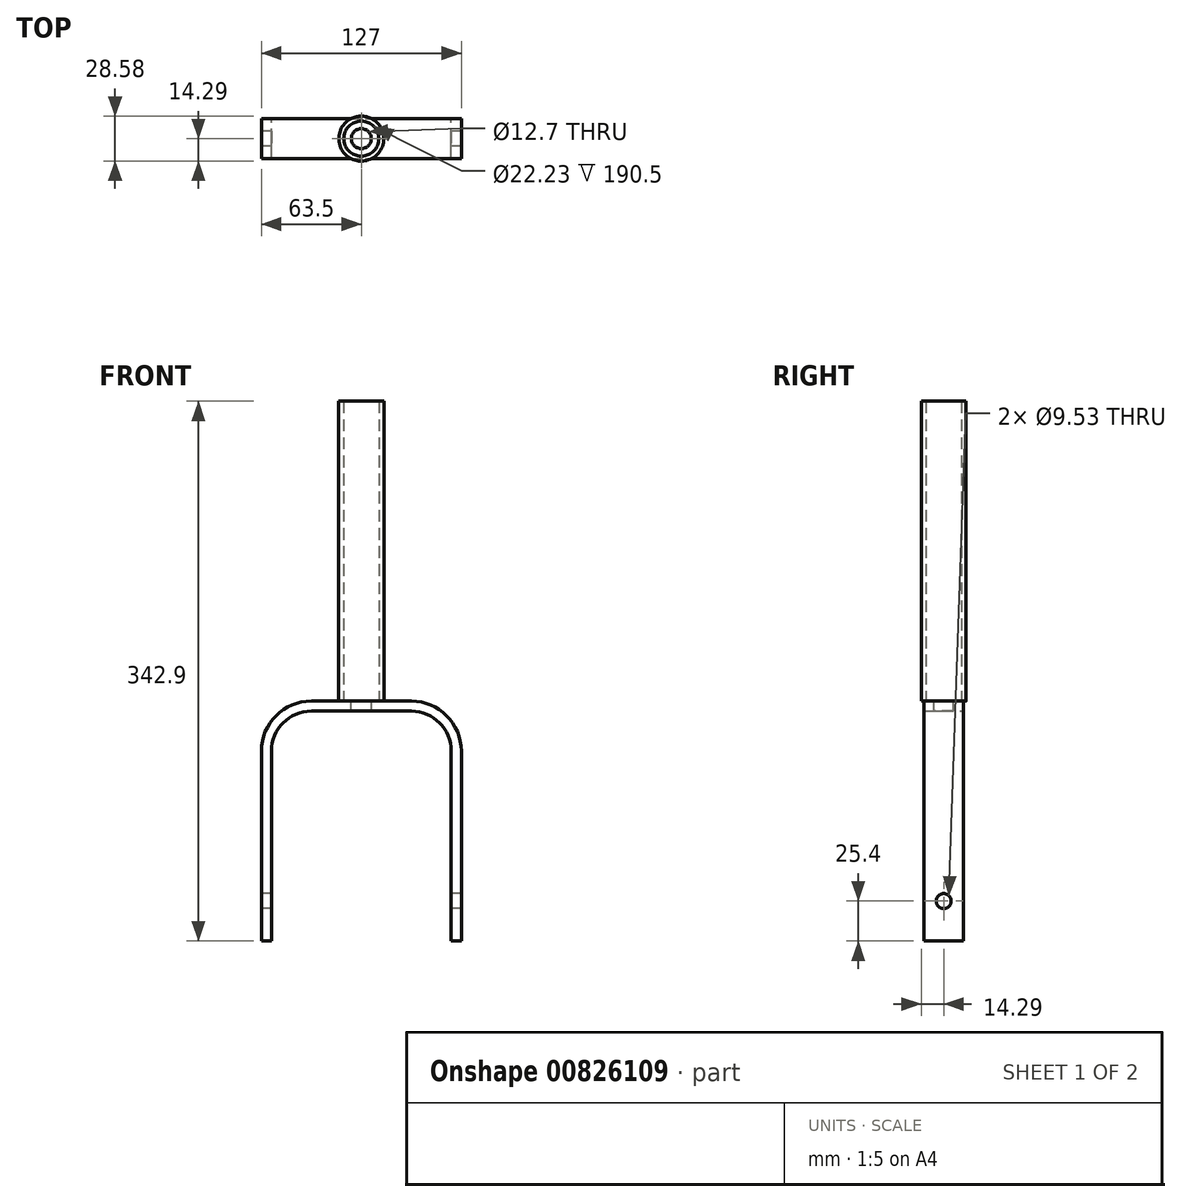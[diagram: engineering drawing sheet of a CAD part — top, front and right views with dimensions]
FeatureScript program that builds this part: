
annotation { "Feature Type Name" : "Feature", "Feature Type Description" : "" }
export const myFeature = defineFeature(function(context is Context, id is Id, definition is map)
    precondition{}
    {
        {
            var Q0;
            Q0=qCreatedBy(makeId("Front.planeOp"),FACE);
            var sketch = newSketch(context, id + "F0", { "sketchPlane" : qUnion([Q0])});
            skLineSegment(sketch, "E0", {"start": v(0, 0) * mm, "end": v(0, 152.4) * mm});
            skLineSegment(sketch, "E1.0", {"start": v(6.35, 0) * mm, "end": v(6.35, 146.05) * mm});
            skLineSegment(sketch, "E2", {"start": v(0, 152.4) * mm, "end": v(127, 152.4) * mm});
            skLineSegment(sketch, "E3", {"start": v(6.35, 146.05) * mm, "end": v(120.65, 146.05) * mm});
            skLineSegment(sketch, "E4", {"start": v(120.65, 146.05) * mm, "end": v(120.65, 0) * mm});
            skLineSegment(sketch, "E5", {"start": v(127, 152.4) * mm, "end": v(127, 0) * mm});
            skLineSegment(sketch, "E6", {"start": v(6.35, 0) * mm, "end": v(0, 0) * mm});
            skLineSegment(sketch, "E7", {"start": v(120.65, 0) * mm, "end": v(127, 0) * mm});
            skSolve(sketch);
        }
        {
            var Q0;
            Q0=makeQuery(id+"F0.imprint","IMPRINT",FACE,{"disambiguationData":[TD([[makeQuery(id+"F0.imprint","IMPRINT",EDGE,{"derivedFrom":sQuery(id+"F0.wireOp",EDGE,"E0")}),-1.0]])]});
            extrude(context, id + "F1", {"entities" : qUnion([Q0]), "endBound" : BoundingType.SYMMETRIC, "depth" : 25.4 * mm, "offsetDistance" : 25.4 * mm});
        }
        {
            var Q0;
            Q0=makeQuery(id+"F1.opExtrude","SWEPT_EDGE",EDGE,{"disambiguationData":[OSD([sQuery(id+"F0.wireOp",EDGE,"E1.0"),sQuery(id+"F0.wireOp",EDGE,"E3")])]});
            var Q1;
            Q1=makeQuery(id+"F1.opExtrude","SWEPT_EDGE",EDGE,{"disambiguationData":[OSD([sQuery(id+"F0.wireOp",EDGE,"E3"),sQuery(id+"F0.wireOp",EDGE,"E4")])]});
            fillet(context, id + "F2", {"entities" : qUnion([Q0, Q1]), "radius" : 25.4 * mm, "tangentPropagation" : true, "allowEdgeOverflow" : false});
        }
        {
            var Q0;
            Q0=makeQuery(id+"F1.opExtrude","SWEPT_EDGE",EDGE,{"disambiguationData":[OSD([sQuery(id+"F0.wireOp",EDGE,"E2"),sQuery(id+"F0.wireOp",EDGE,"E5")])]});
            var Q1;
            Q1=makeQuery(id+"F1.opExtrude","SWEPT_EDGE",EDGE,{"disambiguationData":[OSD([sQuery(id+"F0.wireOp",EDGE,"E0"),sQuery(id+"F0.wireOp",EDGE,"E2")])]});
            fillet(context, id + "F3", {"entities" : qUnion([Q0, Q1]), "radius" : 31.75 * mm, "tangentPropagation" : true, "allowEdgeOverflow" : false});
        }
        {
            var Q0;
            Q0=qCreatedBy(makeId("Right.planeOp"),FACE);
            var sketch = newSketch(context, id + "F4", { "sketchPlane" : qUnion([Q0])});
            skPoint(sketch, "E8", {"position": v(0, 25.4) * mm});
            skSolve(sketch);
        }
        {
            var Q0;
            Q0=sQuery(id+"F4.wireOp",VERTEX,"E8");
            var Q1;
            Q1=makeQuery(id+"F1.opExtrude","SWEPT_BODY",BODY,{"disambiguationData":[OSD([sQuery(id+"F0.wireOp",EDGE,"E0"),sQuery(id+"F0.wireOp",EDGE,"E1.0"),sQuery(id+"F0.wireOp",EDGE,"E2"),sQuery(id+"F0.wireOp",EDGE,"E3"),sQuery(id+"F0.wireOp",EDGE,"E4"),sQuery(id+"F0.wireOp",EDGE,"E5"),sQuery(id+"F0.wireOp",EDGE,"E6"),sQuery(id+"F0.wireOp",EDGE,"E7")])]});
            hole(context, id + "F5", {"style" : HoleStyle.SIMPLE, "endStyle" : HoleEndStyle.THROUGH, "oppositeDirection" : true, "holeDiameter" : 9.52 * mm, "majorDiameter" : 6.35 * mm, "isTappedThrough" : true, "tappedDepth" : 12.7 * mm, "tapClearance" : 3, "locations" : qUnion([Q0]), "scope" : qUnion([Q1])});
        }
        {
            var Q0;
            Q0=makeQuery(id+"F1.opExtrude","SWEPT_FACE",FACE,{"disambiguationData":[OSD([sQuery(id+"F0.wireOp",EDGE,"E2")])]});
            var sketch = newSketch(context, id + "F6", { "sketchPlane" : qUnion([Q0])});
            skPoint(sketch, "E9", {"position": v(63.5, 0) * mm});
            skLineSegment(sketch, "E10", {"start": v(95.25, 0) * mm, "end": v(31.75, 0) * mm, "construction": true});
            skSolve(sketch);
        }
        {
            var Q0;
            Q0=sQuery(id+"F6.wireOp",VERTEX,"E9");
            var Q1;
            Q1=makeQuery(id+"F1.opExtrude","SWEPT_BODY",BODY,{"disambiguationData":[OSD([sQuery(id+"F0.wireOp",EDGE,"E0"),sQuery(id+"F0.wireOp",EDGE,"E1.0"),sQuery(id+"F0.wireOp",EDGE,"E2"),sQuery(id+"F0.wireOp",EDGE,"E3"),sQuery(id+"F0.wireOp",EDGE,"E4"),sQuery(id+"F0.wireOp",EDGE,"E5"),sQuery(id+"F0.wireOp",EDGE,"E6"),sQuery(id+"F0.wireOp",EDGE,"E7")])]});
            hole(context, id + "F7", {"style" : HoleStyle.SIMPLE, "endStyle" : HoleEndStyle.THROUGH, "holeDiameter" : 12.7 * mm, "majorDiameter" : 6.35 * mm, "isTappedThrough" : true, "tappedDepth" : 12.7 * mm, "tapClearance" : 3, "locations" : qUnion([Q0]), "scope" : qUnion([Q1])});
        }
        {
            var Q0;
            Q0=makeQuery(id+"F1.opExtrude","SWEPT_FACE",FACE,{"disambiguationData":[OSD([sQuery(id+"F0.wireOp",EDGE,"E2")])]});
            var sketch = newSketch(context, id + "F8", { "sketchPlane" : qUnion([Q0])});
            skCircle(sketch, "E11", {"center": v(63.5, 0) * mm, "radius": 14.29 * mm});
            skCircle(sketch, "E12", {"center": v(63.5, 0) * mm, "radius": 11.11 * mm});
            skSolve(sketch);
        }
        {
            var Q0;
            Q0=qSketchRegion(id+"F8",true);
            extrude(context, id + "F9", {"entities" : qUnion([Q0]), "operationType" : NewBodyOperationType.ADD, "depth" : 190.5 * mm, "offsetDistance" : 25.4 * mm});
        }
    });
